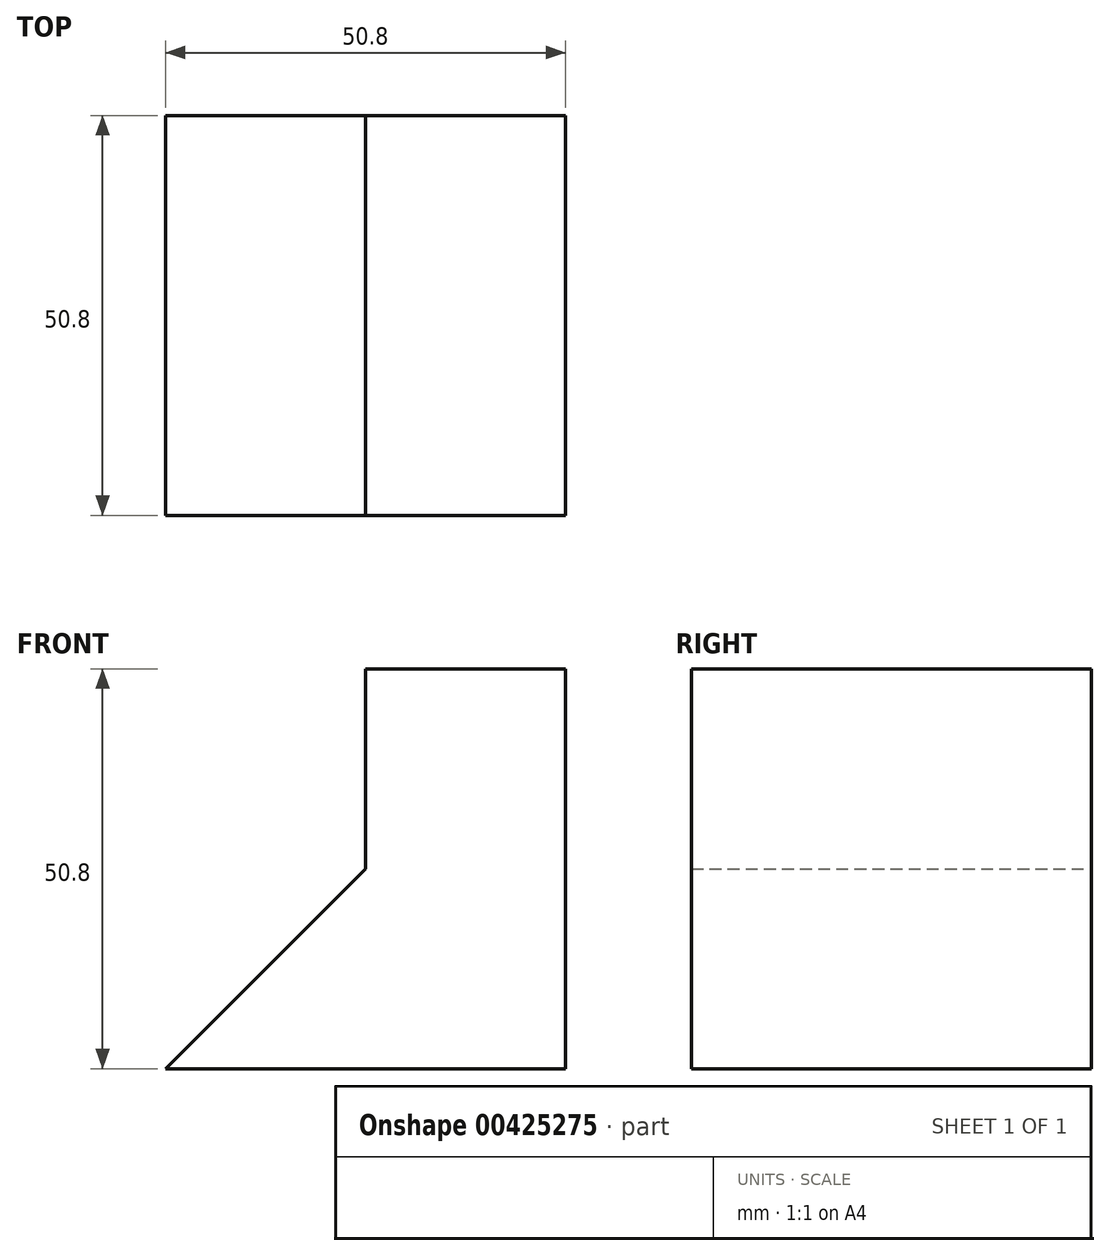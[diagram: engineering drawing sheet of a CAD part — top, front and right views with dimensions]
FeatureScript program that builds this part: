
annotation { "Feature Type Name" : "Feature", "Feature Type Description" : "" }
export const myFeature = defineFeature(function(context is Context, id is Id, definition is map)
    precondition{}
    {
        {
            var Q0;
            Q0=qCreatedBy(makeId("Front.planeOp"),FACE);
            var sketch = newSketch(context, id + "F0", { "sketchPlane" : qUnion([Q0])});
            skLineSegment(sketch, "E0", {"start": v(-16.23, 25.4) * mm, "end": v(9.17, 25.4) * mm});
            skLineSegment(sketch, "E1", {"start": v(9.17, 25.4) * mm, "end": v(9.17, -25.4) * mm});
            skLineSegment(sketch, "E2", {"start": v(-16.23, 25.4) * mm, "end": v(-16.23, 0) * mm});
            skLineSegment(sketch, "E3", {"start": v(9.17, -25.4) * mm, "end": v(-41.63, -25.4) * mm});
            skLineSegment(sketch, "E4", {"start": v(-16.23, 0) * mm, "end": v(-41.63, -25.4) * mm});
            skSolve(sketch);
        }
        {
            var Q0;
            Q0 = qSketchRegion(id + "F0", true);
            extrude(context, id + "F1", {"entities" : qUnion([Q0]), "depth" : 50.8 * mm});
        }
    });
